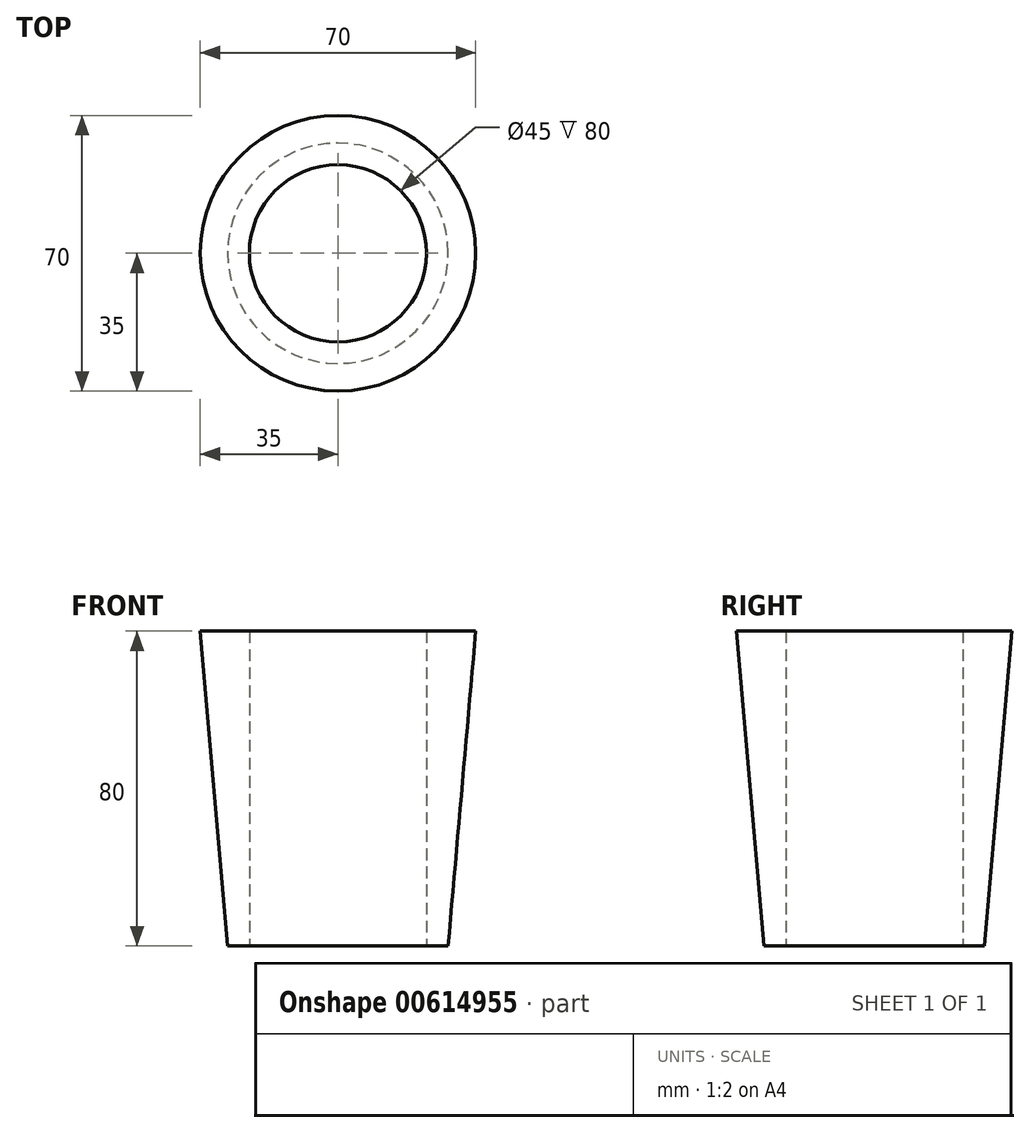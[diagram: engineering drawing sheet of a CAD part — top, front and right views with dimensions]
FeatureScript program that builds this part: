
annotation { "Feature Type Name" : "Feature", "Feature Type Description" : "" }
export const myFeature = defineFeature(function(context is Context, id is Id, definition is map)
    precondition{}
    {
        {
            var Q0;
            Q0=qCreatedBy(makeId("Top.planeOp"),FACE);
            var sketch = newSketch(context, id + "F0", { "sketchPlane" : qUnion([Q0])});
            skCircle(sketch, "E0", {"center": v(0, 0) * mm, "radius": 35 * mm});
            skCircle(sketch, "E1", {"center": v(0, 0) * mm, "radius": 22.5 * mm});
            skSolve(sketch);
        }
        {
            var Q0;
            Q0 = qSketchRegion(id + "F0", true);
            var Q1;
            Q1=makeQuery(id+"F0.imprint","IMPRINT",FACE,{"disambiguationData":[TD([[makeQuery(id+"F0.imprint","IMPRINT",EDGE,{"derivedFrom":sQuery(id+"F0.wireOp",EDGE,"E0")}),1.0]])]});
            extrude(context, id + "F1", {"entities" : qUnion([Q0, Q1]), "depth" : 80 * mm, "offsetDistance" : 25 * mm});
        }
        {
            var Q0;
            Q0=makeQuery(id+"F1.opExtrude","CAP_EDGE",EDGE,{"disambiguationData":[OSD([sQuery(id+"F0.wireOp",EDGE,"E0")])],"isStart":true});
            chamfer(context, id + "F2", {"entities" : qUnion([Q0]), "chamferType" : ChamferType.OFFSET_ANGLE, "width" : 80 * mm, "oppositeDirection" : false, "angle" : 5 * degree, "tangentPropagation" : true});
        }
    });
